# Revit family: HOSPIVAC V4 SIRELLA
name_source: partatom
category: Equipement de génie climatique
revit_build: Autodesk Revit 2018 (Build: 20170223_1515(x64)
units: mm (PartAtom-declared; Revit-internal decimal feet)

## family parameters
Basée sur le plan de construction = Non
Classification = Aucun
Cote de connecteur circulaire = Utiliser le diamètre
Couper avec des vides une fois chargée = Non
Partagée = Non
Point de calcul de pièce = Non
Toujours verticalement = Oui
Type d'élément = Normal

## types (1)
- HOSPIVAC V4 SL100R
    BRANCHEMENT_TERRE = Oui
    COS_PHI = 0
    DEBIT_ASPI_VIDE = 0.0 m³/h
    DESCR_ALIM_X = Alimentation X ; 5G6mm²
    DESCR_ALIM_Y = Alimentation Y ; 5G6mm²
    DESCR_ASPI = Aspiration Vide ; 4 x 90 m³/h ; G 2 " FEM
    DESCR_REFOUL = Aspiration Vide ; 4 x 90 m³/h ; G 1"1/2 MAL
    DESCR_RESERV = Aspiration Réservoir ; G 1"1/2 MAL
    DOUBLE_ALIMENTATION = Oui
    ENTRAXE_SELLETTE = 360 mm  [stored 1.1811 ft]
    FILTR_SL300R = Non
    HAUT = 1008 mm  [stored 3.30709 ft]
    HAUTEUR = 0 mm  [stored 0 ft]
    HAUT_COFF = 695 mm  [stored 2.28018 ft]
    LARG = 860 mm  [stored 2.82152 ft]
    LARGEUR = 0 mm  [stored 0 ft]
    LARG_COFF = 600 mm  [stored 1.9685 ft]
    LONG = 2110 mm  [stored 6.92257 ft]
    LONGUEUR = 0 mm  [stored 0 ft]
    NBR_POLES = 3
    NEUTRE = Oui
    NIVEAU_SONORE(dB(A)) = 0
    OFFSET_HAUT_CANA_FILTR = 968 mm  [stored 3.17585 ft]
    OFFSET_HAUT_FILTR = 1003 mm  [stored 3.29068 ft]
    OFFSET_HAUT_TRAVERSE = 118 mm
    OFFSET_LARG_CANA_FILTR = 267 mm  [stored 0.875984 ft]
    OFFSET_LARG_FILTRE = 77 mm  [stored 0.252625 ft]
    OFFSET_LARG_PPE = 350 mm  [stored 1.14829 ft]
    OFFSET_LONG_COFF = 350 mm  [stored 1.14829 ft]
    OFFSET_LONG_FILTR = 1790 mm  [stored 5.8727 ft]
    OFFSET_TRAVERSE_PPE_A = 295 mm  [stored 0.967848 ft]
    OFFSET_TRAVERSE_PPE_B = 1035 mm  [stored 3.39567 ft]
    POIDS(Kg) = 0 mm  [stored 0 ft]
    PUISS_APPARENTE = 0 VA
    PUISS_APPARENTE_2 = 0 VA
    PUISS_ELECT = 0 kW
    PUISS_ELECT_2 = 0 kW
    TENSION_ALIM = 400 V
    TYPE_COFFRET = COFFRET ELEC STANDARD PM2 : COFFRET PM2 600x800x300
    TYPE_PPE = SIRELLA SLR : SL100.R
    VISIBILITE_SL300R = Oui
    Zone de maintenance 1 = Oui
    Zone de maintenance coffret = Oui
    ØREFOUL = 50 mm  [stored 0.164042 ft]

note: [stored X ft] marks values corroborated as IEEE doubles in the binary element streams (Revit-internal decimal feet)
